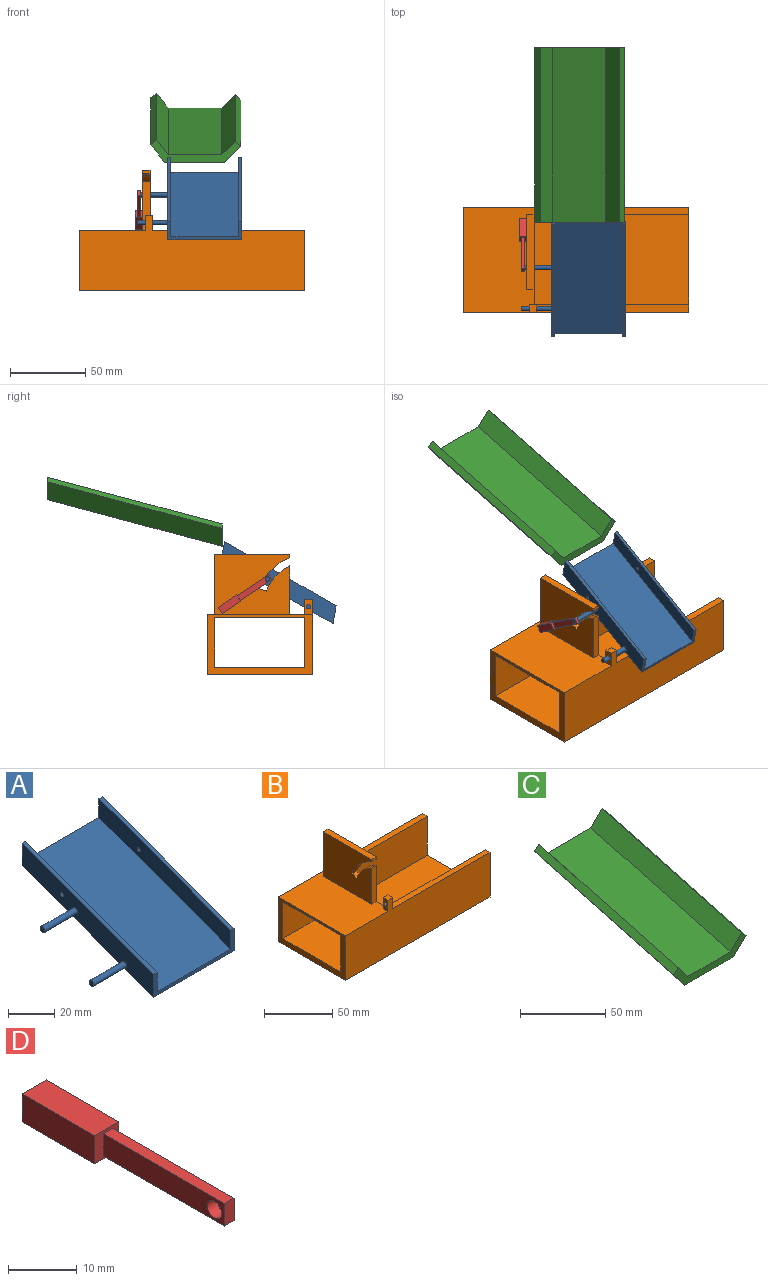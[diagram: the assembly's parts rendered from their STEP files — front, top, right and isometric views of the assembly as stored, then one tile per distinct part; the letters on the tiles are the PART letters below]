
ASSEMBLY  parts=4 mates=3
PART A: 16 faces, bbox 69x80.5x41.3 mm
  f0: plane 49x12mm, normal (0,1,0), area 138mm2, adj f2,f3,f4,f5,f6,f7,f8,f9
  f1: plane 49x12mm, normal (0,-1,0), area 138mm2, adj f2,f3,f4,f5,f6,f7,f8,f9
  f2: plane 80.53x29.31mm, normal (0,-0.34,0.94), area 171.4mm2, adj f0,f1,f3,f9
  f3: plane 80.53x41.31mm, normal (-1,0,0), area 949.1mm2, adj f0,f1,f2,f4,f10,f12,f14
  f4: plane 80.53x49mm, normal (0,0.34,-0.94), area 4199.3mm2, adj f0,f1,f3,f5
  f5: plane 80.53x41.31mm, normal (1,0,0), area 963.2mm2, adj f0,f1,f4,f6,f11
  f6: plane 80.53x29.31mm, normal (0,-0.34,0.94), area 171.4mm2, adj f0,f1,f5,f7
  f7: plane 80.53x39.31mm, normal (-1,0,0), area 802.2mm2, adj f0,f1,f6,f8,f11
  f8: plane 80.53x45mm, normal (0,-0.34,0.94), area 3856.5mm2, adj f0,f1,f7,f9
  f9: plane 80.53x39.31mm, normal (1,0,0), area 802.2mm2, adj f0,f1,f2,f8,f10
  f10: cylinder r=1mm len=2mm, axis (-1,0,0), area 12.6mm2, adj f3,f9
  f11: cylinder r=1mm len=2mm, axis (-1,0,0), area 12.6mm2, adj f5,f7
  f12: cylinder r=1.5mm len=20mm, axis (1,0,0), area 188.5mm2, adj f3,f13
  f13: plane 3x3mm, normal (-1,0,0), area 7.1mm2, adj f12
  f14: cylinder r=1.5mm len=20mm, axis (1,0,0), area 188.5mm2, adj f3,f15
  f15: plane 3x3mm, normal (-1,0,0), area 7.1mm2, adj f14
PART B: 25 faces, bbox 150x70x80 mm
  f0: plane 32.44x5mm, normal (0,-1,0), area 162.2mm2, adj f2,f16,f18,f24
  f1: plane 150x40mm, normal (0,1,0), area 6000mm2, adj f2,f8,f9,f10
  f2: plane 150x70mm, normal (0,0,1), area 3544.9mm2, adj f0,f1,f3,f5,f7,f9,f10,f12
  f3: plane 150x35mm, normal (0,-1,0), area 5155.8mm2, adj f2,f4,f9,f10,f15,f16
  f4: plane 150x60mm, normal (0,0,1), area 9000mm2, adj f3,f5,f9,f10
  f5: plane 150x45mm, normal (0,1,0), area 5205.8mm2, adj f2,f4,f6,f9,f10,f11,f12,f13
  f6: plane 101x5mm, normal (0,0,1), area 505mm2, adj f5,f7,f9,f11
  f7: plane 150x50mm, normal (0,-1,0), area 6050mm2, adj f2,f6,f8,f9,f10,f11,f12,f13
  f8: plane 150x70mm, normal (0,0,-1), area 10500mm2, adj f1,f7,f9,f10
  f9: plane 70x40mm, normal (1,0,0), area 700mm2, adj f1,f2,f3,f4,f5,f6,f7,f8
  f10: plane 70x40mm, normal (-1,0,0), area 820mm2, adj f1,f2,f3,f4,f5,f7,f8,f15
  f11: plane 10x5mm, normal (1,0,0), area 42.9mm2, adj f5,f6,f7,f13,f14
  f12: plane 10x5mm, normal (-1,0,0), area 42.9mm2, adj f2,f5,f7,f13,f14
  f13: plane 5x5mm, normal (0,0,1), area 25mm2, adj f5,f7,f11,f12
  f14: cylinder r=1.5mm len=5mm, axis (1,0,0), area 47.1mm2, adj f11,f12
  f15: plane 60x47.08mm, normal (0,0,-1), area 2824.9mm2, adj f3,f5,f10,f16
  f16: plane 60x42mm, normal (1,0,0), area 1986mm2, adj f0,f2,f3,f5,f15,f17,f19,f20
  f17: plane 40x5mm, normal (0,1,0), area 200mm2, adj f2,f16,f18,f20
  f18: plane 50x40mm, normal (-1,0,0), area 1866mm2, adj f0,f2,f17,f19,f20,f21,f22,f23
  f19: plane 5x2.06mm, normal (0,-1,0), area 10.3mm2, adj f16,f18,f20,f21
  f20: plane 50x5mm, normal (0,0,1), area 250mm2, adj f16,f17,f18,f19
  f21: plane 5x2.09mm, normal (0,-0.42,-0.91), area 11.5mm2, adj f16,f18,f19,f22
  f22: cylinder r=35mm len=19.77mm, axis (-1,0,0), area 138.1mm2, adj f16,f18,f21,f23
  f23: plane 5x4.7mm, normal (0,-0.34,0.94), area 25mm2, adj f16,f18,f22,f24
  f24: cylinder r=30mm len=16.94mm, axis (-1,0,0), area 118.3mm2, adj f0,f16,f18,f23
PART C: 10 faces, bbox 60x115.9x46 mm
  f0: plane 59.95x14.94mm, normal (0,-1,0), area 327.6mm2, adj f2,f3,f4,f5,f6,f7,f8,f9
  f1: plane 59.95x14.94mm, normal (0,1,0), area 327.6mm2, adj f2,f3,f4,f5,f6,f7,f8,f9
  f2: plane 115.91x34.66mm, normal (0.71,-0.18,0.68), area 589.5mm2, adj f0,f1,f3,f9
  f3: plane 115.91x41.47mm, normal (0.68,0.19,-0.71), area 1770.7mm2, adj f0,f1,f2,f4
  f4: plane 115.91x40mm, normal (0,0.26,-0.97), area 4800mm2, adj f0,f1,f3,f5
  f5: plane 115.91x42.94mm, normal (-0.78,0.16,-0.6), area 1761.7mm2, adj f0,f1,f4,f6
  f6: plane 115.91x34.11mm, normal (-0.6,-0.21,0.78), area 592.5mm2, adj f0,f1,f5,f7
  f7: plane 115.91x40.99mm, normal (0.78,-0.16,0.6), area 1472.7mm2, adj f0,f1,f6,f8
  f8: plane 115.91x35.52mm, normal (0,-0.26,0.97), area 4262.6mm2, adj f0,f1,f7,f9
  f9: plane 115.91x40.07mm, normal (-0.68,-0.19,0.71), area 1532.6mm2, adj f0,f1,f2,f8
PART D: 12 faces, bbox 5x40x5 mm
  f0: plane 5x5mm, normal (0,-1,0), area 17mm2, adj f1,f2,f3,f4,f6,f7,f8,f9
  f1: plane 15x5mm, normal (0,0,-1), area 75mm2, adj f0,f2,f4,f5
  f2: plane 15x5mm, normal (1,0,0), area 75mm2, adj f0,f1,f3,f5
  f3: plane 15x5mm, normal (0,0,1), area 75mm2, adj f0,f2,f4,f5
  f4: plane 15x5mm, normal (-1,0,0), area 75mm2, adj f0,f1,f3,f5
  f5: plane 5x5mm, normal (0,1,0), area 25mm2, adj f1,f2,f3,f4
  f6: plane 25x2mm, normal (0,0,1), area 50mm2, adj f0,f7,f9,f10
  f7: plane 25x4mm, normal (-1,0,0), area 92.9mm2, adj f0,f6,f8,f10,f11
  f8: plane 25x2mm, normal (0,0,-1), area 50mm2, adj f0,f7,f9,f10
  f9: plane 25x4mm, normal (1,0,0), area 92.9mm2, adj f0,f6,f8,f10,f11
  f10: plane 4x2mm, normal (0,-1,0), area 8mm2, adj f6,f7,f8,f9
  f11: cylinder r=1.5mm len=3mm, axis (1,0,0), area 18.8mm2, adj f7,f9
PLACE A rot(axis=(1,0,0),10deg) t=(8.5,13.64,43.03)mm
PLACE B at identity fixed
PLACE C t=(1.76,25,45.37)mm
PLACE D rot(axis=(-1,0,0),33.8deg) t=(-32.75,12.46,8.95)mm
MATE revolute A.f12 <-> D.f11  axis (-1,0,0) through (-36,-5.27,23.73)mm
MATE parallel C.f0 <-> B.f1  axis (0,-1,0) through (2.13,25,50)mm
MATE revolute A.f14 <-> B.f14  axis (1,0,0) through (-26,-32.48,5.3)mm
